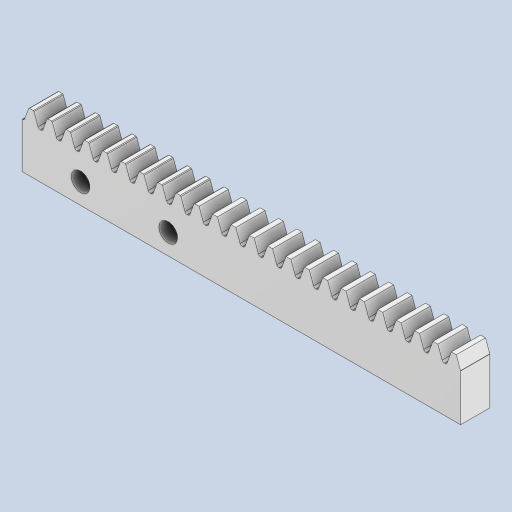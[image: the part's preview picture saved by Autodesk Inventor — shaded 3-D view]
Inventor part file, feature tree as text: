
AUTODESK INVENTOR PART (.ipt)
format: ipt  version: 2023 (Build 270158000, 158)  size: 303,104 bytes
history: native  units: mm
features: extrude x4, sketch x2, pattern_linear x1, chamfer x1
ambient origin geometry x8: Origin, YZ Plane, XZ Plane, XY Plane, X Axis, Y Axis, Z Axis, Center Point
bodies: Solid1 (feature_tree)
feature tree (8):
  extrude  "Extrusion1"  Depth=10.0mm TaperAngle=0.0deg
  extrude  "Extrusion2"  Depth=10.0mm TaperAngle=0.0deg
  pattern_linear  "Rectangular Pattern1"  Spacing1=0.1mm  [1 undecoded]
  chamfer  "面取り1"  Distance=10.0mm
  sketch  "スケッチ4"
  extrude  "押し出し3"  Depth=75.0mm
  extrude  "押し出し4"  Depth=3.0mm
  sketch  "Sketch_1"  dims[d0=5.0mm d1=0.0mm d2=10.0mm d3=0.0mm d4=300.0mm d6=3.142mm d7=10.0mm d9=0.0mm d10=0.1mm d11=2.0mm d12=45.0deg d13=10.0mm d14=75.0mm d23=3.2mm d24=5.7mm d25=3.2mm d26=5.7mm d29=15.0mm d30=3.5mm d31=3.5mm d32=10.0mm d33=5.0mm d34=0.0mm d35=3.0mm d36=0.0mm]
note: 1 required parameter value undecoded (feature->parameter linkage not recoverable at this tier; creation-order binding heuristic only, values carry confidence <= 0.55)
